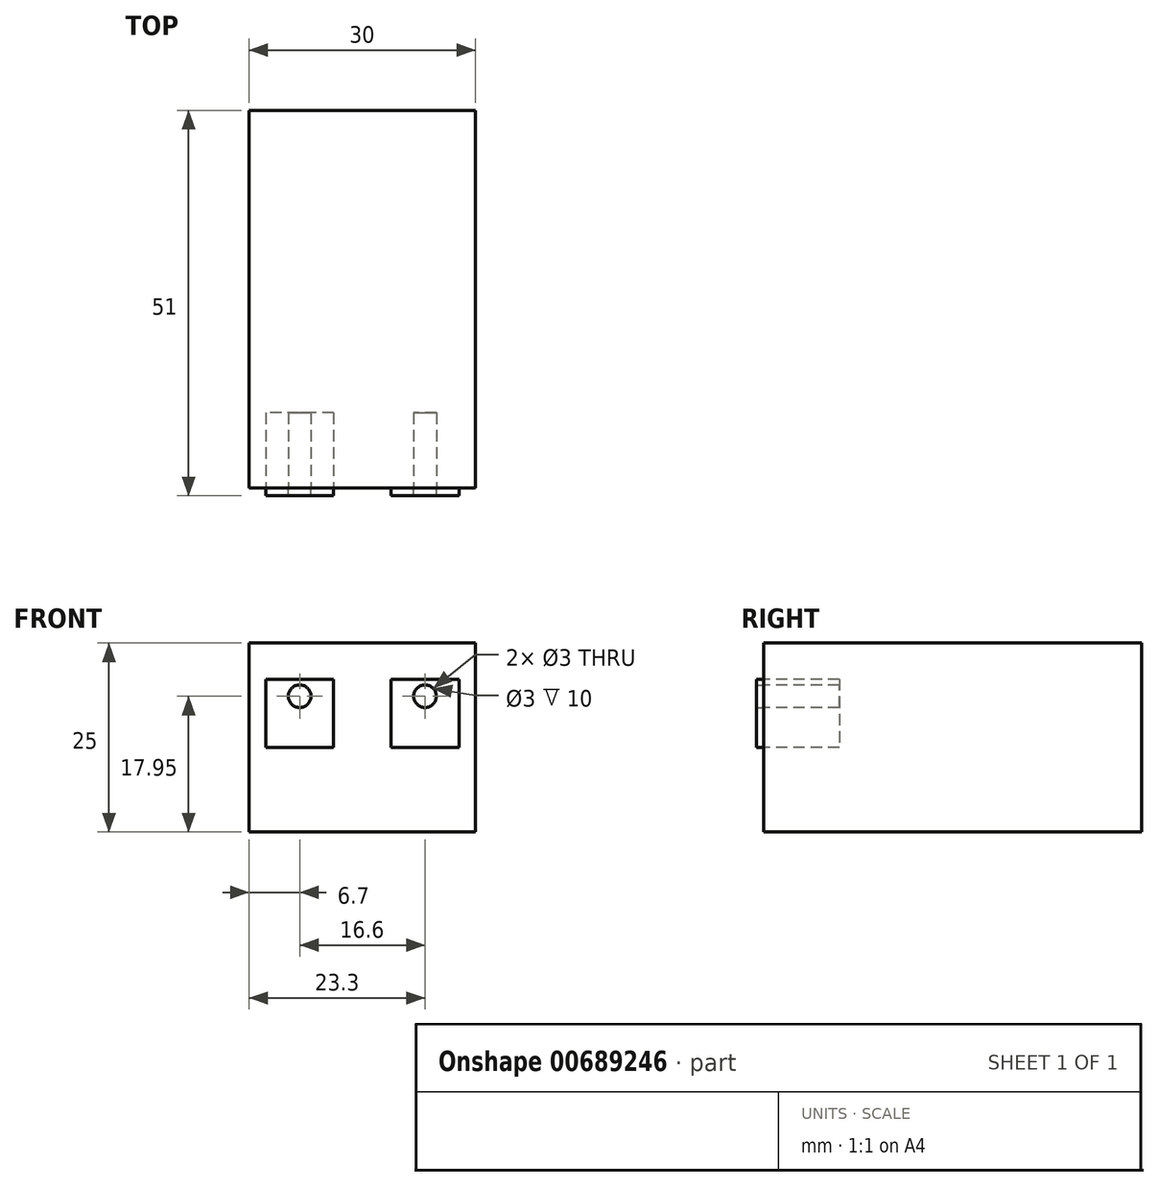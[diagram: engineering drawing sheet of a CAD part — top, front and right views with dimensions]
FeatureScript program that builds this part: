
annotation { "Feature Type Name" : "Feature", "Feature Type Description" : "" }
export const myFeature = defineFeature(function(context is Context, id is Id, definition is map)
    precondition{}
    {
        {
            var Q0;
            Q0=qCreatedBy(makeId("Front.planeOp"),FACE);
            var sketch = newSketch(context, id + "F0", { "sketchPlane" : qUnion([Q0])});
            skLineSegment(sketch, "E0.bottom", {"start": v(15, 12.5) * mm, "end": v(-15, 12.5) * mm});
            skLineSegment(sketch, "E0.top", {"start": v(15, -12.5) * mm, "end": v(-15, -12.5) * mm});
            skLineSegment(sketch, "E0.left", {"start": v(15, 12.5) * mm, "end": v(15, -12.5) * mm});
            skLineSegment(sketch, "E0.right", {"start": v(-15, 12.5) * mm, "end": v(-15, -12.5) * mm});
            skPoint(sketch, "E0.middle", {"position": v(0, 0) * mm});
            skSolve(sketch);
        }
        {
            var Q0;
            Q0=makeQuery(id+"F0.imprint","IMPRINT",FACE,{"disambiguationData":[TD([[makeQuery(id+"F0.imprint","IMPRINT",EDGE,{"derivedFrom":sQuery(id+"F0.wireOp",EDGE,"E0.bottom")}),1.0]])]});
            extrude(context, id + "F1", {"entities" : qUnion([Q0]), "oppositeDirection" : true, "depth" : 50 * mm, "offsetDistance" : 25 * mm});
        }
        {
            var Q0;
            Q0=makeQuery(id+"F1.opExtrude","CAP_FACE",FACE,{"disambiguationData":[OSD([sQuery(id+"F0.wireOp",EDGE,"E0.bottom"),sQuery(id+"F0.wireOp",EDGE,"E0.top"),sQuery(id+"F0.wireOp",EDGE,"E0.left"),sQuery(id+"F0.wireOp",EDGE,"E0.right")])],"isStart":true});
            var sketch = newSketch(context, id + "F2", { "sketchPlane" : qUnion([Q0])});
            skLineSegment(sketch, "E1", {"start": v(0, 7.07) * mm, "end": v(7.07, 0) * mm, "construction": true});
            skLineSegment(sketch, "E2", {"start": v(7.07, 0) * mm, "end": v(0, -7.07) * mm, "construction": true});
            skLineSegment(sketch, "E3", {"start": v(0, -7.07) * mm, "end": v(-7.07, 0) * mm, "construction": true});
            skLineSegment(sketch, "E4", {"start": v(-7.07, 0) * mm, "end": v(0, 7.07) * mm, "construction": true});
            skLineSegment(sketch, "E5.bottom", {"start": v(-3.8, 7.7) * mm, "end": v(-12.8, 7.7) * mm});
            skLineSegment(sketch, "E5.top", {"start": v(-3.8, -1.3) * mm, "end": v(-12.8, -1.3) * mm});
            skLineSegment(sketch, "E5.left", {"start": v(-3.8, 7.7) * mm, "end": v(-3.8, -1.3) * mm});
            skLineSegment(sketch, "E5.right", {"start": v(-12.8, 7.7) * mm, "end": v(-12.8, -1.3) * mm});
            skPoint(sketch, "E5.middle", {"position": v(-8.3, 3.2) * mm});
            skLineSegment(sketch, "E6.bottom", {"start": v(3.8, 7.7) * mm, "end": v(12.8, 7.7) * mm});
            skLineSegment(sketch, "E6.top", {"start": v(3.8, -1.3) * mm, "end": v(12.8, -1.3) * mm});
            skLineSegment(sketch, "E6.left", {"start": v(3.8, 7.7) * mm, "end": v(3.8, -1.3) * mm});
            skLineSegment(sketch, "E6.right", {"start": v(12.8, 7.7) * mm, "end": v(12.8, -1.3) * mm});
            skPoint(sketch, "E6.middle", {"position": v(8.3, 3.2) * mm});
            skCircle(sketch, "E7", {"center": v(8.3, 5.45) * mm, "radius": 1.5 * mm});
            skCircle(sketch, "E8.MirrorC", {"center": v(-8.3, 5.45) * mm, "radius": 1.5 * mm});
            skSolve(sketch);
        }
        {
            var Q0;
            Q0=makeQuery(id+"F2.imprint","IMPRINT",FACE,{"disambiguationData":[TD([[makeQuery(id+"F2.imprint","IMPRINT",EDGE,{"derivedFrom":sQuery(id+"F2.wireOp",EDGE,"E8.MirrorC")}),-1.0]])]});
            var Q1;
            Q1=makeQuery(id+"F2.imprint","IMPRINT",FACE,{"disambiguationData":[TD([[makeQuery(id+"F2.imprint","IMPRINT",EDGE,{"derivedFrom":sQuery(id+"F2.wireOp",EDGE,"E7")}),1.0]])]});
            var Q2;
            Q2=sQuery(id+"F2.wireOp",EDGE,"E7");
            var Q3;
            Q3=sQuery(id+"F2.wireOp",EDGE,"E8.MirrorC");
            extrude(context, id + "F3", {"entities" : qUnion([Q0, Q1]), "operationType" : NewBodyOperationType.REMOVE, "surfaceEntities" : qUnion([Q2, Q3]), "oppositeDirection" : true, "depth" : 10 * mm, "offsetDistance" : 25 * mm});
        }
        {
            var Q0;
            Q0=makeQuery(id+"F2.imprint","IMPRINT",FACE,{"disambiguationData":[TD([[makeQuery(id+"F2.imprint","IMPRINT",EDGE,{"derivedFrom":sQuery(id+"F2.wireOp",EDGE,"E5.bottom")}),1.0]])]});
            var Q1;
            Q1=makeQuery(id+"F2.imprint","IMPRINT",FACE,{"disambiguationData":[TD([[makeQuery(id+"F2.imprint","IMPRINT",EDGE,{"derivedFrom":sQuery(id+"F2.wireOp",EDGE,"E6.bottom")}),-1.0]])]});
            extrude(context, id + "F4", {"entities" : qUnion([Q0, Q1]), "depth" : 1 * mm, "offsetDistance" : 25 * mm});
        }
    });
